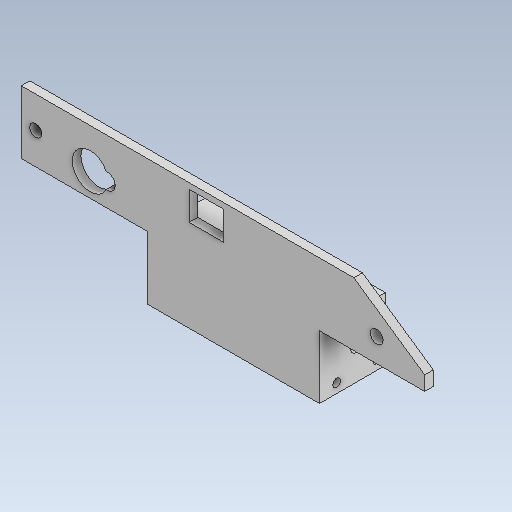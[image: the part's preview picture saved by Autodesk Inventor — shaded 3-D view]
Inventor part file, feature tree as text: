
AUTODESK INVENTOR PART (.ipt)
format: ipt  version: 2020 (Build 240168000, 168)  size: 226,816 bytes
history: native  units: mm
features: reference x28, other x8, sketch x6, extrude x5, hole x3
ambient origin geometry x8: Origin, YZ Plane, XZ Plane, XY Plane, X Axis, Y Axis, Z Axis, Center Point
bodies: Body1 (feature_tree)
feature tree (50):
  other  "Bryła1"
  extrude  "Wyciągnięcie proste1"  Depth=0.25mm
  extrude  "Wyciągnięcie proste2"  Depth=12.5mm
  sketch  "Szkic4"
  hole  "Otwór2"  [1 undecoded]
  extrude  "Wyciągnięcie proste3"  Depth=2.0mm
  extrude  "Wyciągnięcie proste4"  Depth=10.0mm
  hole  "Otwór3"  [1 undecoded]
  extrude  "Wyciągnięcie proste5"  Depth=10.0mm
  hole  "Otwór1"  [1 undecoded]
  reference  "Odniesienie1"
  reference  "Odniesienie2"
  reference  "Odniesienie3"
  reference  "Odniesienie4"
  reference  "Odniesienie5"
  reference  "Odniesienie6"
  reference  "Odniesienie7"
  reference  "Odniesienie8"
  reference  "Odniesienie9"
  reference  "Odniesienie10"
  reference  "Odniesienie11"
  reference  "Odniesienie12"
  reference  "Odniesienie13"
  sketch  "Szkic2"
  sketch  "Szkic5"
  reference  "Odniesienie14"
  reference  "Odniesienie15"
  reference  "Odniesienie16"
  reference  "Odniesienie17"
  reference  "Odniesienie18"
  reference  "Odniesienie19"
  reference  "Odniesienie20"
  reference  "Odniesienie21"
  reference  "Odniesienie22"
  reference  "Odniesienie23"
  reference  "Odniesienie24"
  reference  "Odniesienie25"
  sketch  "Szkic6"
  sketch  "Szkic7"
  reference  "Odniesienie26"
  reference  "Odniesienie27"
  reference  "Odniesienie28"
  sketch  "Szkic8"
  other  "<userpath>\Desktop\3d\scanning-robot\Assembly1.iam"
  other  "Assembly1.iam"
  other  "base:1"
  other  "Tower Pro MG90S Micro servo:2"
  other  "Крышка корпуса:1"
  other  "AS 1112 (2) - Metryczny M4  Typ 5:1"
  other  "coupler:1"
note: 3 required parameter values undecoded (feature->parameter linkage not recoverable at this tier; creation-order binding heuristic only, values carry confidence <= 0.55)
